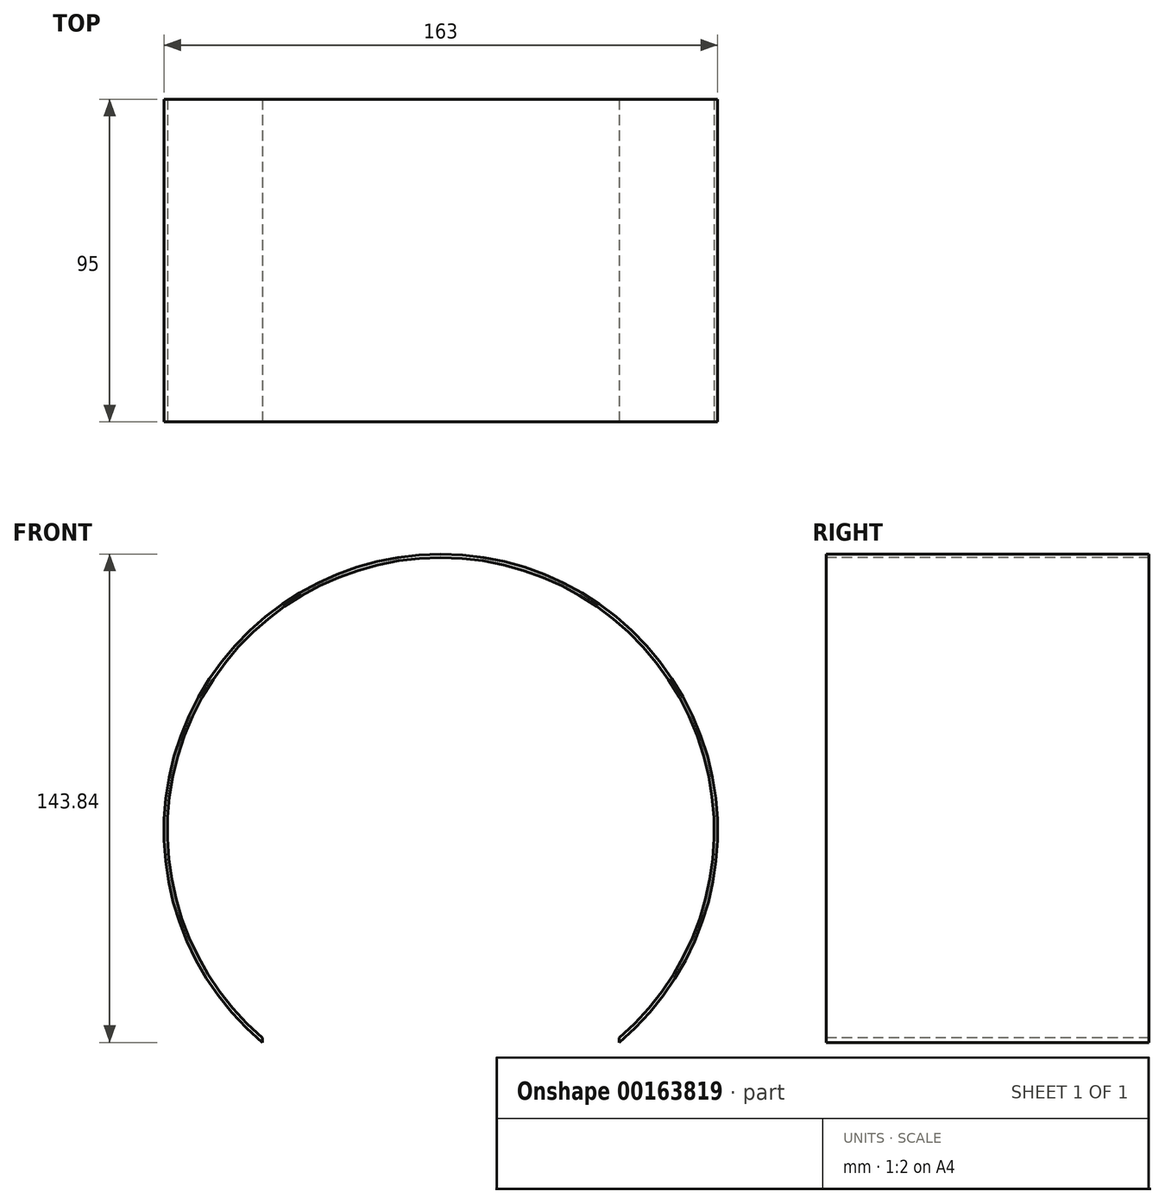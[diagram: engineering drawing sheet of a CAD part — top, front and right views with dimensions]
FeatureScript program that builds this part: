
annotation { "Feature Type Name" : "Feature", "Feature Type Description" : "" }
export const myFeature = defineFeature(function(context is Context, id is Id, definition is map)
    precondition{}
    {
        {
            var Q0;
            Q0=qCreatedBy(makeId("Front.planeOp"),FACE);
            var sketch = newSketch(context, id + "F0", { "sketchPlane" : qUnion([Q0])});
            skArc(sketch, "E0", {"start": v(52.5, -62.34) * mm, "mid": v(0, 81.5) * mm, "end": v(-52.5, -62.34) * mm});
            skArc(sketch, "E1", {"start": v(52.5, -61.02) * mm, "mid": v(0, 80.5) * mm, "end": v(-52.5, -61.02) * mm});
            skLineSegment(sketch, "E2.left", {"start": v(52.5, -62.34) * mm, "end": v(52.5, -61.02) * mm});
            skLineSegment(sketch, "E2.right", {"start": v(-52.5, -62.34) * mm, "end": v(-52.5, -61.02) * mm});
            skPoint(sketch, "E2.top.end.orphan", {"position": v(-52.5, 100.5) * mm});
            skPoint(sketch, "E3.orphan", {"position": v(52.5, 100.5) * mm});
            skPoint(sketch, "E2.bottom.start.orphan", {"position": v(52.5, -100.5) * mm});
            skPoint(sketch, "E4.orphan", {"position": v(-52.5, -100.5) * mm});
            skSolve(sketch);
        }
        {
            var Q0;
            Q0=makeQuery(id+"F0.imprint","IMPRINT",FACE,{"disambiguationData":[TD([[makeQuery(id+"F0.imprint","IMPRINT",EDGE,{"derivedFrom":sQuery(id+"F0.wireOp",EDGE,"E0")}),1.0]])]});
            extrude(context, id + "F1", {"entities" : qUnion([Q0]), "oppositeDirection" : true, "depth" : 95 * mm});
        }
    });
